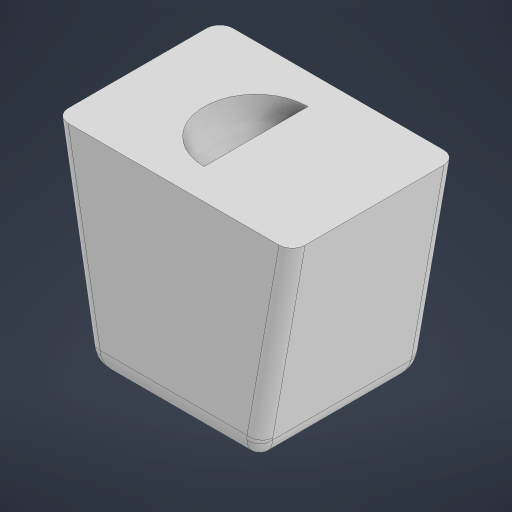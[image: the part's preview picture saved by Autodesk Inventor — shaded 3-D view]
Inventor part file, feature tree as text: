
AUTODESK INVENTOR PART (.ipt)
format: ipt  version: 2024.1 (Build 281209000, 209)  size: 446,464 bytes
history: native  units: mm
features: fillet x2, sketch x2, extrude x1, revolve x1, other x1
ambient origin geometry x8: Origin, YZ Plane, XZ Plane, XY Plane, X Axis, Y Axis, Z Axis, Center Point
bodies: Solid1 (feature_tree)
feature tree (7):
  extrude  "Extrusion1"  Depth=15.933mm
  fillet  "Fillet1"  Radius=12.64mm
  fillet  "Fillet2"  Radius=12.7mm
  revolve  "Revolution1"  [1 undecoded]
  other  "Work Axis1"
  sketch  "Sketch1"  dims[d0=2.82mm d1=15.933mm d2=12.64mm d3=12.7mm d4=0.0mm]
  sketch  "Sketch2"  dims[d5=2.0mm d6=1.0mm d7=4.0mm d8=135.0deg]
note: 1 required parameter value undecoded (feature->parameter linkage not recoverable at this tier; creation-order binding heuristic only, values carry confidence <= 0.55)
